# Revit family: Drain_Floor_Adjustable_12_Inch_Diameter-Zurn-Z526-Heavy-Duty
name_source: partatom
category: Plumbing Fixtures
units: mm (PartAtom-declared; Revit-internal decimal feet)

## family parameters
Always vertical = Yes
Cut with Voids When Loaded = No
Maintain Annotation Orientation = No
OmniClass Number = 23.70.50.21.24.14
OmniClass Title = Deck Waste Water Drains
Part Type = Normal
Room Calculation Point = No
Round Connector Dimension = Use Radius
Shared = No
Work Plane-Based = No

## types (11) — shared parameters
Approx. Weight (Lbs) = 60 "
Assembly Code = D2030300
CW Connection = No
Default Elevation = 25 "
Description = 12-1/4 [311] DIAMETER TOP ADJUSTABLE HEAVY-DUTY DRAIN
Grate Open Area Sq.in = 33 "
HW Connection = No
Main Material = Iron - Zurn - Cast - Painted - Blue
Manufacturer = Zurn Water, LLC
Manufacurer Brand = Zurn
Model = Z526
Modified Date = 11/21/2025
Product Documentation Link = https://files.zurn.com
Product Page URL = https://www.zurn.com
Product data url = https://www.bimobject.com
URL = www.zurn.com
Vent Connection = No
WFU = 1
Waste Connection = Yes
Width = 15 "
zero-valued in all types: CWFU, HWFU

## per-type parameters (varying)
| type | A_ Pipe Size (Actual-Inner) | A_ Pipe Size (Actual-Outer) | A_ Pipe Size (Nominal) | Body Height_E | Connector Radius | Frame and Grate | Top Diameter | Top inner Diameter | Type Comments | Z-Grate | ZN Height Difference | ZN-Grate |
| Z526-2NH | 2.067 " | 2.375 " | 2 " | 5.25 " | 1 " | Iron - Zurn - Cast - Painted - Blue | 12.25 " | 11.18 " | Z526-2 Inch No-Hub Outlet | Yes | 0 " | No |
| Z526-2NL | 2.067 " | 2.375 " | 2 " | 4.625 " | 1 " | Bronze - Zurn - Polished Nickel | 12.938 " | 11.878 " | ZN526-2 Inch Neo-Loc Outlet | No | 0.188 " | Yes |
| Z526-3NH | 3.068 " | 2.375 " | 3 " | 5.25 " | 1.5 " | Bronze - Zurn - Polished Nickel | 12.938 " | 11.878 " | ZN526-3 Inch No-Hub Outlet | No | 0.188 " | Yes |
| Z526-3IC | 3.068 " | 3.5 " | 3 " | 5.25 " | 1.5 " | Bronze - Zurn - Polished Nickel | 12.938 " | 11.878 " | ZN526-3 Inch Inside Caulk Outlet | No | 0.188 " | Yes |
| Z526-3NL | 3.068 " | 3.5 " | 3 " | 4.625 " | 1.5 " | Bronze - Zurn - Polished Nickel | 12.938 " | 11.878 " | ZN526-3 Inch Neo-Loc Outlet | No | 0.188 " | Yes |
| Z526-4NH | 4.026 " | 3.5 " | 4 " | 5.25 " | 2 " | Bronze - Zurn - Polished Nickel | 12.938 " | 11.878 " | ZN526-4 Inch No-Hub Outlet | No | 0.188 " | Yes |
| Z526-4IC | 4.026 " | 4.5 " | 4 " | 5.25 " | 2 " | Bronze - Zurn - Polished Nickel | 12.938 " | 11.878 " | ZN526-4 Inch Inside Caulk Outlet | No | 0.188 " | Yes |
| Z526-4NL | 4.026 " | 4.5 " | 4 " | 4.625 " | 2 " | Bronze - Zurn - Polished Nickel | 12.938 " | 11.878 " | ZN526-2 Inch Neo-Loc Outlet | No | 0.188 " | Yes |
| Z526-6NH | 6.065 " | 4.5 " | 6 " | 5.25 " | 3 " | Bronze - Zurn - Polished Nickel | 12.938 " | 11.878 " | ZN526-6 Inch No-Hub Outlet | No | 0.188 " | Yes |
| Z526-8NH | 7.981 " | 6.625 " | 8 " | 5.25 " | 4 " | Bronze - Zurn - Polished Nickel | 12.938 " | 11.878 " | ZN526-8 Inch No-Hub Outlet | No | 0.188 " | Yes |
| ZN526-2NH | 2.067 " | 2.375 " | 2 " | 5.25 " | 1 " | Bronze - Zurn - Polished Nickel | 12.938 " | 11.878 " | ZN526-2 Inch No-Hub Outlet | No | 0.188 " | Yes |

## geometry (parser evidence)
native form markers: Sweep x6
no freeform markers — native parametric forms only
